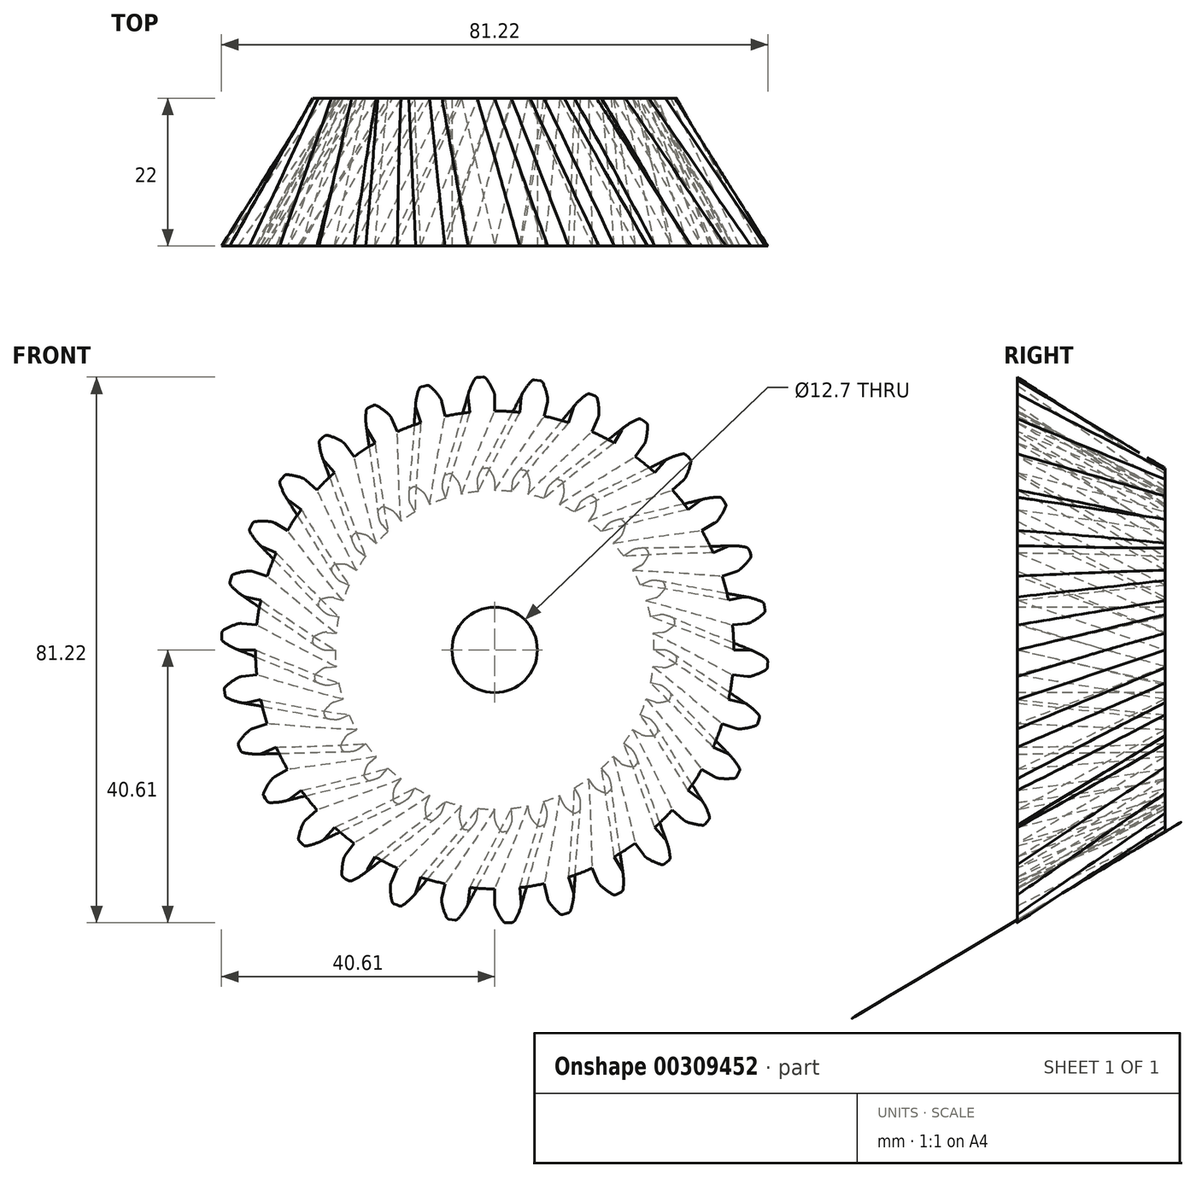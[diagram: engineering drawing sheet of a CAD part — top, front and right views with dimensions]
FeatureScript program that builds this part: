
annotation { "Feature Type Name" : "Feature", "Feature Type Description" : "" }
export const myFeature = defineFeature(function(context is Context, id is Id, definition is map)
    precondition{}
    {
        {
            var Q0;
            Q0=qCreatedBy(makeId("Front.planeOp"),FACE);
            var sketch = newSketch(context, id + "F0", { "sketchPlane" : qUnion([Q0])});
            skCircle(sketch, "E0", {"center": v(0, 0) * mm, "radius": 23.71 * mm});
            skArc(sketch, "E1.trimOffspring", {"start": v(-0.14, 25.74) * mm, "mid": v(-0.44, 26.31) * mm, "end": v(-0.8, 26.85) * mm});
            skLineSegment(sketch, "E2", {"start": v(0, 25.08) * mm, "end": v(0, 23.71) * mm});
            skLineSegment(sketch, "E3", {"start": v(-1.22, 27.06) * mm, "end": v(-1.42, 27.06) * mm});
            skLineSegment(sketch, "E4.MirrorCS", {"start": v(-1.62, 27.04) * mm, "end": v(-1.42, 27.06) * mm});
            skArc(sketch, "E5.MirrorCS", {"start": v(-2.55, 25.61) * mm, "mid": v(-2.31, 26.22) * mm, "end": v(-2.02, 26.79) * mm});
            skLineSegment(sketch, "E6.MirrorCS", {"start": v(-2.62, 24.94) * mm, "end": v(-2.48, 23.58) * mm});
            skPoint(sketch, "E7.visualSharp", {"position": v(-2.66, 25.26) * mm});
            skArc(sketch, "E7.filletArc", {"start": v(-2.55, 25.61) * mm, "mid": v(-2.62, 25.28) * mm, "end": v(-2.62, 24.94) * mm});
            skPoint(sketch, "E8.visualSharp", {"position": v(0, 25.4) * mm});
            skArc(sketch, "E8.filletArc", {"start": v(0, 25.08) * mm, "mid": v(-0.04, 25.42) * mm, "end": v(-0.14, 25.74) * mm});
            skPoint(sketch, "E9.visualSharp", {"position": v(-1.88, 27.02) * mm});
            skArc(sketch, "E9.filletArc", {"start": v(-1.62, 27.04) * mm, "mid": v(-1.85, 26.97) * mm, "end": v(-2.02, 26.79) * mm});
            skPoint(sketch, "E10.visualSharp", {"position": v(-0.96, 27.07) * mm});
            skArc(sketch, "E10.filletArc", {"start": v(-0.8, 26.85) * mm, "mid": v(-0.98, 27.01) * mm, "end": v(-1.22, 27.06) * mm});
            skSolve(sketch);
        }
        {
            var Q0;
            Q0=qCreatedBy(makeId("Front.planeOp"),FACE);
            cPlane(context, id + "F1", {"entities" : qUnion([Q0]), "cplaneType" : CPlaneType.OFFSET, "offset" : 22 * mm, "width" : 152.4 * mm, "height" : 152.4 * mm});
        }
        {
            var Q0;
            Q0=qCreatedBy(id+"F1.planeOp",FACE);
            var sketch = newSketch(context, id + "F2", { "sketchPlane" : qUnion([Q0])});
            skCircle(sketch, "E11", {"center": v(0, 0) * mm, "radius": 35.56 * mm});
            skArc(sketch, "E12.trimOffspring", {"start": v(-0.13, 38.42) * mm, "mid": v(-0.64, 39.44) * mm, "end": v(-1.28, 40.4) * mm});
            skLineSegment(sketch, "E13", {"start": v(0, 37.79) * mm, "end": v(0, 35.56) * mm});
            skLineSegment(sketch, "E14", {"start": v(-1.7, 40.6) * mm, "end": v(-2.13, 40.6) * mm});
            skLineSegment(sketch, "E15.MirrorCS", {"start": v(-2.55, 40.56) * mm, "end": v(-2.13, 40.6) * mm});
            skArc(sketch, "E16.MirrorCS", {"start": v(-3.89, 38.22) * mm, "mid": v(-3.48, 39.3) * mm, "end": v(-2.95, 40.31) * mm});
            skLineSegment(sketch, "E17.MirrorCS", {"start": v(-3.95, 37.58) * mm, "end": v(-3.72, 35.37) * mm});
            skPoint(sketch, "E18.visualSharp", {"position": v(-3.98, 37.9) * mm});
            skArc(sketch, "E18.filletArc", {"start": v(-3.89, 38.22) * mm, "mid": v(-3.95, 37.9) * mm, "end": v(-3.95, 37.58) * mm});
            skPoint(sketch, "E19.visualSharp", {"position": v(0, 38.1) * mm});
            skArc(sketch, "E19.filletArc", {"start": v(0, 37.79) * mm, "mid": v(-0.03, 38.1) * mm, "end": v(-0.13, 38.42) * mm});
            skPoint(sketch, "E20.visualSharp", {"position": v(-2.81, 40.54) * mm});
            skArc(sketch, "E20.filletArc", {"start": v(-2.55, 40.56) * mm, "mid": v(-2.78, 40.49) * mm, "end": v(-2.95, 40.31) * mm});
            skPoint(sketch, "E21.visualSharp", {"position": v(-1.44, 40.61) * mm});
            skArc(sketch, "E21.filletArc", {"start": v(-1.28, 40.4) * mm, "mid": v(-1.46, 40.56) * mm, "end": v(-1.7, 40.6) * mm});
            skLineSegment(sketch, "E22.1.0", {"start": v(-10.93, 39.14) * mm, "end": v(-10.52, 39.26) * mm});
            skLineSegment(sketch, "E22.1.1", {"start": v(-10.1, 39.36) * mm, "end": v(-10.52, 39.26) * mm});
            skArc(sketch, "E22.1.2", {"start": v(-9.65, 39.25) * mm, "mid": v(-9.86, 39.37) * mm, "end": v(-10.1, 39.36) * mm});
            skArc(sketch, "E22.1.3", {"start": v(-10.93, 39.14) * mm, "mid": v(-11.14, 39.02) * mm, "end": v(-11.27, 38.82) * mm});
            skArc(sketch, "E22.1.4", {"start": v(-11.75, 36.58) * mm, "mid": v(-11.58, 37.71) * mm, "end": v(-11.27, 38.82) * mm});
            skArc(sketch, "E22.1.5", {"start": v(-8.11, 37.55) * mm, "mid": v(-8.83, 38.45) * mm, "end": v(-9.65, 39.25) * mm});
            skArc(sketch, "E22.1.6", {"start": v(-7.86, 36.96) * mm, "mid": v(-7.95, 37.27) * mm, "end": v(-8.11, 37.55) * mm});
            skArc(sketch, "E22.1.7", {"start": v(-11.75, 36.58) * mm, "mid": v(-11.75, 36.25) * mm, "end": v(-11.68, 35.94) * mm});
            skLineSegment(sketch, "E22.1.8", {"start": v(-11.68, 35.94) * mm, "end": v(-10.99, 33.82) * mm});
            skLineSegment(sketch, "E22.1.9", {"start": v(-7.86, 36.96) * mm, "end": v(-7.4, 34.78) * mm});
            skLineSegment(sketch, "E22.2.0", {"start": v(-18.83, 36.01) * mm, "end": v(-18.45, 36.22) * mm});
            skLineSegment(sketch, "E22.2.1", {"start": v(-18.07, 36.4) * mm, "end": v(-18.45, 36.22) * mm});
            skArc(sketch, "E22.2.2", {"start": v(-17.6, 36.4) * mm, "mid": v(-17.83, 36.45) * mm, "end": v(-18.07, 36.4) * mm});
            skArc(sketch, "E22.2.3", {"start": v(-18.83, 36.01) * mm, "mid": v(-19.01, 35.85) * mm, "end": v(-19.1, 35.63) * mm});
            skArc(sketch, "E22.2.4", {"start": v(-19.1, 33.33) * mm, "mid": v(-19.17, 34.48) * mm, "end": v(-19.1, 35.63) * mm});
            skArc(sketch, "E22.2.5", {"start": v(-15.74, 35.04) * mm, "mid": v(-16.63, 35.77) * mm, "end": v(-17.6, 36.4) * mm});
            skArc(sketch, "E22.2.6", {"start": v(-15.37, 34.52) * mm, "mid": v(-15.53, 34.8) * mm, "end": v(-15.74, 35.04) * mm});
            skArc(sketch, "E22.2.7", {"start": v(-19.1, 33.33) * mm, "mid": v(-19.03, 33.02) * mm, "end": v(-18.9, 32.73) * mm});
            skLineSegment(sketch, "E22.2.8", {"start": v(-18.9, 32.73) * mm, "end": v(-17.78, 30.8) * mm});
            skLineSegment(sketch, "E22.2.9", {"start": v(-15.37, 34.52) * mm, "end": v(-14.46, 32.49) * mm});
            skLineSegment(sketch, "E22.3.0", {"start": v(-25.9, 31.31) * mm, "end": v(-25.58, 31.59) * mm});
            skLineSegment(sketch, "E22.3.1", {"start": v(-25.24, 31.85) * mm, "end": v(-25.58, 31.59) * mm});
            skArc(sketch, "E22.3.2", {"start": v(-24.78, 31.94) * mm, "mid": v(-25.02, 31.95) * mm, "end": v(-25.24, 31.85) * mm});
            skArc(sketch, "E22.3.3", {"start": v(-25.9, 31.31) * mm, "mid": v(-26.05, 31.12) * mm, "end": v(-26.09, 30.88) * mm});
            skArc(sketch, "E22.3.4", {"start": v(-25.61, 28.63) * mm, "mid": v(-25.92, 29.74) * mm, "end": v(-26.09, 30.88) * mm});
            skArc(sketch, "E22.3.5", {"start": v(-22.68, 31) * mm, "mid": v(-23.7, 31.53) * mm, "end": v(-24.78, 31.94) * mm});
            skArc(sketch, "E22.3.6", {"start": v(-22.21, 30.57) * mm, "mid": v(-22.43, 30.81) * mm, "end": v(-22.68, 31) * mm});
            skArc(sketch, "E22.3.7", {"start": v(-25.61, 28.63) * mm, "mid": v(-25.48, 28.34) * mm, "end": v(-25.29, 28.08) * mm});
            skLineSegment(sketch, "E22.3.8", {"start": v(-25.29, 28.08) * mm, "end": v(-23.8, 26.43) * mm});
            skLineSegment(sketch, "E22.3.9", {"start": v(-22.21, 30.57) * mm, "end": v(-20.9, 28.77) * mm});
            skLineSegment(sketch, "E22.4.0", {"start": v(-31.85, 25.24) * mm, "end": v(-31.59, 25.58) * mm});
            skLineSegment(sketch, "E22.4.1", {"start": v(-31.31, 25.9) * mm, "end": v(-31.59, 25.58) * mm});
            skArc(sketch, "E22.4.2", {"start": v(-30.88, 26.09) * mm, "mid": v(-31.12, 26.05) * mm, "end": v(-31.31, 25.9) * mm});
            skArc(sketch, "E22.4.3", {"start": v(-31.85, 25.24) * mm, "mid": v(-31.95, 25.02) * mm, "end": v(-31.94, 24.78) * mm});
            skArc(sketch, "E22.4.4", {"start": v(-31, 22.68) * mm, "mid": v(-31.53, 23.7) * mm, "end": v(-31.94, 24.78) * mm});
            skArc(sketch, "E22.4.5", {"start": v(-28.63, 25.61) * mm, "mid": v(-29.74, 25.92) * mm, "end": v(-30.88, 26.09) * mm});
            skArc(sketch, "E22.4.6", {"start": v(-28.08, 25.29) * mm, "mid": v(-28.34, 25.48) * mm, "end": v(-28.63, 25.61) * mm});
            skArc(sketch, "E22.4.7", {"start": v(-31, 22.68) * mm, "mid": v(-30.81, 22.43) * mm, "end": v(-30.57, 22.21) * mm});
            skLineSegment(sketch, "E22.4.8", {"start": v(-30.57, 22.21) * mm, "end": v(-28.77, 20.9) * mm});
            skLineSegment(sketch, "E22.4.9", {"start": v(-28.08, 25.29) * mm, "end": v(-26.43, 23.8) * mm});
            skLineSegment(sketch, "E22.5.0", {"start": v(-36.4, 18.07) * mm, "end": v(-36.22, 18.45) * mm});
            skLineSegment(sketch, "E22.5.1", {"start": v(-36.01, 18.83) * mm, "end": v(-36.22, 18.45) * mm});
            skArc(sketch, "E22.5.2", {"start": v(-35.63, 19.1) * mm, "mid": v(-35.85, 19.01) * mm, "end": v(-36.01, 18.83) * mm});
            skArc(sketch, "E22.5.3", {"start": v(-36.4, 18.07) * mm, "mid": v(-36.45, 17.83) * mm, "end": v(-36.4, 17.6) * mm});
            skArc(sketch, "E22.5.4", {"start": v(-35.04, 15.74) * mm, "mid": v(-35.77, 16.63) * mm, "end": v(-36.4, 17.6) * mm});
            skArc(sketch, "E22.5.5", {"start": v(-33.33, 19.1) * mm, "mid": v(-34.48, 19.17) * mm, "end": v(-35.63, 19.1) * mm});
            skArc(sketch, "E22.5.6", {"start": v(-32.73, 18.9) * mm, "mid": v(-33.02, 19.03) * mm, "end": v(-33.33, 19.1) * mm});
            skArc(sketch, "E22.5.7", {"start": v(-35.04, 15.74) * mm, "mid": v(-34.8, 15.53) * mm, "end": v(-34.52, 15.37) * mm});
            skLineSegment(sketch, "E22.5.8", {"start": v(-34.52, 15.37) * mm, "end": v(-32.49, 14.46) * mm});
            skLineSegment(sketch, "E22.5.9", {"start": v(-32.73, 18.9) * mm, "end": v(-30.8, 17.78) * mm});
            skLineSegment(sketch, "E22.6.0", {"start": v(-39.36, 10.1) * mm, "end": v(-39.26, 10.52) * mm});
            skLineSegment(sketch, "E22.6.1", {"start": v(-39.14, 10.93) * mm, "end": v(-39.26, 10.52) * mm});
            skArc(sketch, "E22.6.2", {"start": v(-38.82, 11.27) * mm, "mid": v(-39.02, 11.14) * mm, "end": v(-39.14, 10.93) * mm});
            skArc(sketch, "E22.6.3", {"start": v(-39.36, 10.1) * mm, "mid": v(-39.37, 9.86) * mm, "end": v(-39.25, 9.65) * mm});
            skArc(sketch, "E22.6.4", {"start": v(-37.55, 8.11) * mm, "mid": v(-38.45, 8.83) * mm, "end": v(-39.25, 9.65) * mm});
            skArc(sketch, "E22.6.5", {"start": v(-36.58, 11.75) * mm, "mid": v(-37.71, 11.58) * mm, "end": v(-38.82, 11.27) * mm});
            skArc(sketch, "E22.6.6", {"start": v(-35.94, 11.68) * mm, "mid": v(-36.25, 11.75) * mm, "end": v(-36.58, 11.75) * mm});
            skArc(sketch, "E22.6.7", {"start": v(-37.55, 8.11) * mm, "mid": v(-37.27, 7.95) * mm, "end": v(-36.96, 7.86) * mm});
            skLineSegment(sketch, "E22.6.8", {"start": v(-36.96, 7.86) * mm, "end": v(-34.78, 7.4) * mm});
            skLineSegment(sketch, "E22.6.9", {"start": v(-35.94, 11.68) * mm, "end": v(-33.82, 10.99) * mm});
            skLineSegment(sketch, "E22.7.0", {"start": v(-40.6, 1.7) * mm, "end": v(-40.6, 2.13) * mm});
            skLineSegment(sketch, "E22.7.1", {"start": v(-40.56, 2.55) * mm, "end": v(-40.6, 2.13) * mm});
            skArc(sketch, "E22.7.2", {"start": v(-40.31, 2.95) * mm, "mid": v(-40.49, 2.78) * mm, "end": v(-40.56, 2.55) * mm});
            skArc(sketch, "E22.7.3", {"start": v(-40.6, 1.7) * mm, "mid": v(-40.56, 1.46) * mm, "end": v(-40.4, 1.28) * mm});
            skArc(sketch, "E22.7.4", {"start": v(-38.42, 0.13) * mm, "mid": v(-39.44, 0.64) * mm, "end": v(-40.4, 1.28) * mm});
            skArc(sketch, "E22.7.5", {"start": v(-38.22, 3.89) * mm, "mid": v(-39.3, 3.48) * mm, "end": v(-40.31, 2.95) * mm});
            skArc(sketch, "E22.7.6", {"start": v(-37.58, 3.95) * mm, "mid": v(-37.9, 3.95) * mm, "end": v(-38.22, 3.89) * mm});
            skArc(sketch, "E22.7.7", {"start": v(-38.42, 0.13) * mm, "mid": v(-38.1, 0.03) * mm, "end": v(-37.79, 0) * mm});
            skLineSegment(sketch, "E22.7.8", {"start": v(-37.79, 0) * mm, "end": v(-35.56, 0) * mm});
            skLineSegment(sketch, "E22.7.9", {"start": v(-37.58, 3.95) * mm, "end": v(-35.37, 3.72) * mm});
            skLineSegment(sketch, "E22.8.0", {"start": v(-40.07, -6.78) * mm, "end": v(-40.15, -6.36) * mm});
            skLineSegment(sketch, "E22.8.1", {"start": v(-40.2, -5.93) * mm, "end": v(-40.15, -6.36) * mm});
            skArc(sketch, "E22.8.2", {"start": v(-40.05, -5.5) * mm, "mid": v(-40.18, -5.7) * mm, "end": v(-40.2, -5.93) * mm});
            skArc(sketch, "E22.8.3", {"start": v(-40.07, -6.78) * mm, "mid": v(-39.97, -7) * mm, "end": v(-39.79, -7.15) * mm});
            skArc(sketch, "E22.8.4", {"start": v(-37.6, -7.86) * mm, "mid": v(-38.72, -7.57) * mm, "end": v(-39.79, -7.15) * mm});
            skArc(sketch, "E22.8.5", {"start": v(-38.2, -4.14) * mm, "mid": v(-39.16, -4.76) * mm, "end": v(-40.05, -5.5) * mm});
            skArc(sketch, "E22.8.6", {"start": v(-37.58, -3.95) * mm, "mid": v(-37.9, -4.02) * mm, "end": v(-38.2, -4.14) * mm});
            skArc(sketch, "E22.8.7", {"start": v(-37.6, -7.86) * mm, "mid": v(-37.28, -7.9) * mm, "end": v(-36.96, -7.86) * mm});
            skLineSegment(sketch, "E22.8.8", {"start": v(-36.96, -7.86) * mm, "end": v(-34.78, -7.4) * mm});
            skLineSegment(sketch, "E22.8.9", {"start": v(-37.58, -3.95) * mm, "end": v(-35.37, -3.72) * mm});
            skLineSegment(sketch, "E22.9.0", {"start": v(-37.79, -14.96) * mm, "end": v(-37.95, -14.57) * mm});
            skLineSegment(sketch, "E22.9.1", {"start": v(-38.1, -14.16) * mm, "end": v(-37.95, -14.57) * mm});
            skArc(sketch, "E22.9.2", {"start": v(-38.03, -13.7) * mm, "mid": v(-38.12, -13.92) * mm, "end": v(-38.1, -14.16) * mm});
            skArc(sketch, "E22.9.3", {"start": v(-37.79, -14.96) * mm, "mid": v(-37.64, -15.16) * mm, "end": v(-37.43, -15.27) * mm});
            skArc(sketch, "E22.9.4", {"start": v(-35.15, -15.5) * mm, "mid": v(-36.3, -15.46) * mm, "end": v(-37.43, -15.27) * mm});
            skArc(sketch, "E22.9.5", {"start": v(-36.5, -12) * mm, "mid": v(-37.32, -12.8) * mm, "end": v(-38.03, -13.7) * mm});
            skArc(sketch, "E22.9.6", {"start": v(-35.94, -11.68) * mm, "mid": v(-36.23, -11.8) * mm, "end": v(-36.5, -12) * mm});
            skArc(sketch, "E22.9.7", {"start": v(-35.15, -15.5) * mm, "mid": v(-34.83, -15.47) * mm, "end": v(-34.52, -15.37) * mm});
            skLineSegment(sketch, "E22.9.8", {"start": v(-34.52, -15.37) * mm, "end": v(-32.49, -14.46) * mm});
            skLineSegment(sketch, "E22.9.9", {"start": v(-35.94, -11.68) * mm, "end": v(-33.82, -10.99) * mm});
            skLineSegment(sketch, "E22.10.0", {"start": v(-33.85, -22.5) * mm, "end": v(-34.09, -22.14) * mm});
            skLineSegment(sketch, "E22.10.1", {"start": v(-34.32, -21.77) * mm, "end": v(-34.09, -22.14) * mm});
            skArc(sketch, "E22.10.2", {"start": v(-34.35, -21.3) * mm, "mid": v(-34.4, -21.54) * mm, "end": v(-34.32, -21.77) * mm});
            skArc(sketch, "E22.10.3", {"start": v(-33.85, -22.5) * mm, "mid": v(-33.67, -22.66) * mm, "end": v(-33.44, -22.72) * mm});
            skArc(sketch, "E22.10.4", {"start": v(-31.15, -22.48) * mm, "mid": v(-32.29, -22.67) * mm, "end": v(-33.44, -22.72) * mm});
            skArc(sketch, "E22.10.5", {"start": v(-33.2, -19.32) * mm, "mid": v(-33.84, -20.28) * mm, "end": v(-34.35, -21.3) * mm});
            skArc(sketch, "E22.10.6", {"start": v(-32.73, -18.9) * mm, "mid": v(-32.99, -19.08) * mm, "end": v(-33.2, -19.32) * mm});
            skArc(sketch, "E22.10.7", {"start": v(-31.15, -22.48) * mm, "mid": v(-30.85, -22.37) * mm, "end": v(-30.57, -22.21) * mm});
            skLineSegment(sketch, "E22.10.8", {"start": v(-30.57, -22.21) * mm, "end": v(-28.77, -20.9) * mm});
            skLineSegment(sketch, "E22.10.9", {"start": v(-32.73, -18.9) * mm, "end": v(-30.8, -17.78) * mm});
            skLineSegment(sketch, "E22.11.0", {"start": v(-28.43, -29.04) * mm, "end": v(-28.74, -28.74) * mm});
            skLineSegment(sketch, "E22.11.1", {"start": v(-29.04, -28.43) * mm, "end": v(-28.74, -28.74) * mm});
            skArc(sketch, "E22.11.2", {"start": v(-29.17, -27.98) * mm, "mid": v(-29.16, -28.22) * mm, "end": v(-29.04, -28.43) * mm});
            skArc(sketch, "E22.11.3", {"start": v(-28.43, -29.04) * mm, "mid": v(-28.22, -29.16) * mm, "end": v(-27.98, -29.17) * mm});
            skArc(sketch, "E22.11.4", {"start": v(-25.8, -28.46) * mm, "mid": v(-26.87, -28.88) * mm, "end": v(-27.98, -29.17) * mm});
            skArc(sketch, "E22.11.5", {"start": v(-28.46, -25.8) * mm, "mid": v(-28.88, -26.87) * mm, "end": v(-29.17, -27.98) * mm});
            skArc(sketch, "E22.11.6", {"start": v(-28.08, -25.29) * mm, "mid": v(-28.3, -25.52) * mm, "end": v(-28.46, -25.8) * mm});
            skArc(sketch, "E22.11.7", {"start": v(-25.8, -28.46) * mm, "mid": v(-25.52, -28.3) * mm, "end": v(-25.29, -28.08) * mm});
            skLineSegment(sketch, "E22.11.8", {"start": v(-25.29, -28.08) * mm, "end": v(-23.8, -26.43) * mm});
            skLineSegment(sketch, "E22.11.9", {"start": v(-28.08, -25.29) * mm, "end": v(-26.43, -23.8) * mm});
            skLineSegment(sketch, "E22.12.0", {"start": v(-21.77, -34.32) * mm, "end": v(-22.14, -34.09) * mm});
            skLineSegment(sketch, "E22.12.1", {"start": v(-22.5, -33.85) * mm, "end": v(-22.14, -34.09) * mm});
            skArc(sketch, "E22.12.2", {"start": v(-22.72, -33.44) * mm, "mid": v(-22.66, -33.67) * mm, "end": v(-22.5, -33.85) * mm});
            skArc(sketch, "E22.12.3", {"start": v(-21.77, -34.32) * mm, "mid": v(-21.54, -34.4) * mm, "end": v(-21.3, -34.35) * mm});
            skArc(sketch, "E22.12.4", {"start": v(-19.32, -33.2) * mm, "mid": v(-20.28, -33.84) * mm, "end": v(-21.3, -34.35) * mm});
            skArc(sketch, "E22.12.5", {"start": v(-22.48, -31.15) * mm, "mid": v(-22.67, -32.29) * mm, "end": v(-22.72, -33.44) * mm});
            skArc(sketch, "E22.12.6", {"start": v(-22.21, -30.57) * mm, "mid": v(-22.37, -30.85) * mm, "end": v(-22.48, -31.15) * mm});
            skArc(sketch, "E22.12.7", {"start": v(-19.32, -33.2) * mm, "mid": v(-19.08, -32.99) * mm, "end": v(-18.9, -32.73) * mm});
            skLineSegment(sketch, "E22.12.8", {"start": v(-18.9, -32.73) * mm, "end": v(-17.78, -30.8) * mm});
            skLineSegment(sketch, "E22.12.9", {"start": v(-22.21, -30.57) * mm, "end": v(-20.9, -28.77) * mm});
            skLineSegment(sketch, "E22.13.0", {"start": v(-14.16, -38.1) * mm, "end": v(-14.57, -37.95) * mm});
            skLineSegment(sketch, "E22.13.1", {"start": v(-14.96, -37.79) * mm, "end": v(-14.57, -37.95) * mm});
            skArc(sketch, "E22.13.2", {"start": v(-15.27, -37.43) * mm, "mid": v(-15.16, -37.64) * mm, "end": v(-14.96, -37.79) * mm});
            skArc(sketch, "E22.13.3", {"start": v(-14.16, -38.1) * mm, "mid": v(-13.92, -38.12) * mm, "end": v(-13.7, -38.03) * mm});
            skArc(sketch, "E22.13.4", {"start": v(-12, -36.5) * mm, "mid": v(-12.8, -37.32) * mm, "end": v(-13.7, -38.03) * mm});
            skArc(sketch, "E22.13.5", {"start": v(-15.5, -35.15) * mm, "mid": v(-15.46, -36.3) * mm, "end": v(-15.27, -37.43) * mm});
            skArc(sketch, "E22.13.6", {"start": v(-15.37, -34.52) * mm, "mid": v(-15.47, -34.83) * mm, "end": v(-15.5, -35.15) * mm});
            skArc(sketch, "E22.13.7", {"start": v(-12, -36.5) * mm, "mid": v(-11.8, -36.23) * mm, "end": v(-11.68, -35.94) * mm});
            skLineSegment(sketch, "E22.13.8", {"start": v(-11.68, -35.94) * mm, "end": v(-10.99, -33.82) * mm});
            skLineSegment(sketch, "E22.13.9", {"start": v(-15.37, -34.52) * mm, "end": v(-14.46, -32.49) * mm});
            skLineSegment(sketch, "E22.14.0", {"start": v(-5.93, -40.2) * mm, "end": v(-6.36, -40.15) * mm});
            skLineSegment(sketch, "E22.14.1", {"start": v(-6.78, -40.07) * mm, "end": v(-6.36, -40.15) * mm});
            skArc(sketch, "E22.14.2", {"start": v(-7.15, -39.79) * mm, "mid": v(-7, -39.97) * mm, "end": v(-6.78, -40.07) * mm});
            skArc(sketch, "E22.14.3", {"start": v(-5.93, -40.2) * mm, "mid": v(-5.7, -40.18) * mm, "end": v(-5.5, -40.05) * mm});
            skArc(sketch, "E22.14.4", {"start": v(-4.14, -38.2) * mm, "mid": v(-4.76, -39.16) * mm, "end": v(-5.5, -40.05) * mm});
            skArc(sketch, "E22.14.5", {"start": v(-7.86, -37.6) * mm, "mid": v(-7.57, -38.72) * mm, "end": v(-7.15, -39.79) * mm});
            skArc(sketch, "E22.14.6", {"start": v(-7.86, -36.96) * mm, "mid": v(-7.9, -37.28) * mm, "end": v(-7.86, -37.6) * mm});
            skArc(sketch, "E22.14.7", {"start": v(-4.14, -38.2) * mm, "mid": v(-4.02, -37.9) * mm, "end": v(-3.95, -37.58) * mm});
            skLineSegment(sketch, "E22.14.8", {"start": v(-3.95, -37.58) * mm, "end": v(-3.72, -35.37) * mm});
            skLineSegment(sketch, "E22.14.9", {"start": v(-7.86, -36.96) * mm, "end": v(-7.4, -34.78) * mm});
            skLineSegment(sketch, "E22.15.0", {"start": v(2.55, -40.56) * mm, "end": v(2.13, -40.6) * mm});
            skLineSegment(sketch, "E22.15.1", {"start": v(1.7, -40.6) * mm, "end": v(2.13, -40.6) * mm});
            skArc(sketch, "E22.15.2", {"start": v(1.28, -40.4) * mm, "mid": v(1.46, -40.56) * mm, "end": v(1.7, -40.6) * mm});
            skArc(sketch, "E22.15.3", {"start": v(2.55, -40.56) * mm, "mid": v(2.78, -40.49) * mm, "end": v(2.95, -40.31) * mm});
            skArc(sketch, "E22.15.4", {"start": v(3.89, -38.22) * mm, "mid": v(3.48, -39.3) * mm, "end": v(2.95, -40.31) * mm});
            skArc(sketch, "E22.15.5", {"start": v(0.13, -38.42) * mm, "mid": v(0.64, -39.44) * mm, "end": v(1.28, -40.4) * mm});
            skArc(sketch, "E22.15.6", {"start": v(0, -37.79) * mm, "mid": v(0.03, -38.1) * mm, "end": v(0.13, -38.42) * mm});
            skArc(sketch, "E22.15.7", {"start": v(3.89, -38.22) * mm, "mid": v(3.95, -37.9) * mm, "end": v(3.95, -37.58) * mm});
            skLineSegment(sketch, "E22.15.8", {"start": v(3.95, -37.58) * mm, "end": v(3.72, -35.37) * mm});
            skLineSegment(sketch, "E22.15.9", {"start": v(0, -37.79) * mm, "end": v(0, -35.56) * mm});
            skLineSegment(sketch, "E22.16.0", {"start": v(10.93, -39.14) * mm, "end": v(10.52, -39.26) * mm});
            skLineSegment(sketch, "E22.16.1", {"start": v(10.1, -39.36) * mm, "end": v(10.52, -39.26) * mm});
            skArc(sketch, "E22.16.2", {"start": v(9.65, -39.25) * mm, "mid": v(9.86, -39.37) * mm, "end": v(10.1, -39.36) * mm});
            skArc(sketch, "E22.16.3", {"start": v(10.93, -39.14) * mm, "mid": v(11.14, -39.02) * mm, "end": v(11.27, -38.82) * mm});
            skArc(sketch, "E22.16.4", {"start": v(11.75, -36.58) * mm, "mid": v(11.58, -37.71) * mm, "end": v(11.27, -38.82) * mm});
            skArc(sketch, "E22.16.5", {"start": v(8.11, -37.55) * mm, "mid": v(8.83, -38.45) * mm, "end": v(9.65, -39.25) * mm});
            skArc(sketch, "E22.16.6", {"start": v(7.86, -36.96) * mm, "mid": v(7.95, -37.27) * mm, "end": v(8.11, -37.55) * mm});
            skArc(sketch, "E22.16.7", {"start": v(11.75, -36.58) * mm, "mid": v(11.75, -36.25) * mm, "end": v(11.68, -35.94) * mm});
            skLineSegment(sketch, "E22.16.8", {"start": v(11.68, -35.94) * mm, "end": v(10.99, -33.82) * mm});
            skLineSegment(sketch, "E22.16.9", {"start": v(7.86, -36.96) * mm, "end": v(7.4, -34.78) * mm});
            skLineSegment(sketch, "E22.17.0", {"start": v(18.83, -36.01) * mm, "end": v(18.45, -36.22) * mm});
            skLineSegment(sketch, "E22.17.1", {"start": v(18.07, -36.4) * mm, "end": v(18.45, -36.22) * mm});
            skArc(sketch, "E22.17.2", {"start": v(17.6, -36.4) * mm, "mid": v(17.83, -36.45) * mm, "end": v(18.07, -36.4) * mm});
            skArc(sketch, "E22.17.3", {"start": v(18.83, -36.01) * mm, "mid": v(19.01, -35.85) * mm, "end": v(19.1, -35.63) * mm});
            skArc(sketch, "E22.17.4", {"start": v(19.1, -33.33) * mm, "mid": v(19.17, -34.48) * mm, "end": v(19.1, -35.63) * mm});
            skArc(sketch, "E22.17.5", {"start": v(15.74, -35.04) * mm, "mid": v(16.63, -35.77) * mm, "end": v(17.6, -36.4) * mm});
            skArc(sketch, "E22.17.6", {"start": v(15.37, -34.52) * mm, "mid": v(15.53, -34.8) * mm, "end": v(15.74, -35.04) * mm});
            skArc(sketch, "E22.17.7", {"start": v(19.1, -33.33) * mm, "mid": v(19.03, -33.02) * mm, "end": v(18.9, -32.73) * mm});
            skLineSegment(sketch, "E22.17.8", {"start": v(18.9, -32.73) * mm, "end": v(17.78, -30.8) * mm});
            skLineSegment(sketch, "E22.17.9", {"start": v(15.37, -34.52) * mm, "end": v(14.46, -32.49) * mm});
            skLineSegment(sketch, "E22.18.0", {"start": v(25.9, -31.31) * mm, "end": v(25.58, -31.59) * mm});
            skLineSegment(sketch, "E22.18.1", {"start": v(25.24, -31.85) * mm, "end": v(25.58, -31.59) * mm});
            skArc(sketch, "E22.18.2", {"start": v(24.78, -31.94) * mm, "mid": v(25.02, -31.95) * mm, "end": v(25.24, -31.85) * mm});
            skArc(sketch, "E22.18.3", {"start": v(25.9, -31.31) * mm, "mid": v(26.05, -31.12) * mm, "end": v(26.09, -30.88) * mm});
            skArc(sketch, "E22.18.4", {"start": v(25.61, -28.63) * mm, "mid": v(25.92, -29.74) * mm, "end": v(26.09, -30.88) * mm});
            skArc(sketch, "E22.18.5", {"start": v(22.68, -31) * mm, "mid": v(23.7, -31.53) * mm, "end": v(24.78, -31.94) * mm});
            skArc(sketch, "E22.18.6", {"start": v(22.21, -30.57) * mm, "mid": v(22.43, -30.81) * mm, "end": v(22.68, -31) * mm});
            skArc(sketch, "E22.18.7", {"start": v(25.61, -28.63) * mm, "mid": v(25.48, -28.34) * mm, "end": v(25.29, -28.08) * mm});
            skLineSegment(sketch, "E22.18.8", {"start": v(25.29, -28.08) * mm, "end": v(23.8, -26.43) * mm});
            skLineSegment(sketch, "E22.18.9", {"start": v(22.21, -30.57) * mm, "end": v(20.9, -28.77) * mm});
            skLineSegment(sketch, "E22.19.0", {"start": v(31.85, -25.24) * mm, "end": v(31.59, -25.58) * mm});
            skLineSegment(sketch, "E22.19.1", {"start": v(31.31, -25.9) * mm, "end": v(31.59, -25.58) * mm});
            skArc(sketch, "E22.19.2", {"start": v(30.88, -26.09) * mm, "mid": v(31.12, -26.05) * mm, "end": v(31.31, -25.9) * mm});
            skArc(sketch, "E22.19.3", {"start": v(31.85, -25.24) * mm, "mid": v(31.95, -25.02) * mm, "end": v(31.94, -24.78) * mm});
            skArc(sketch, "E22.19.4", {"start": v(31, -22.68) * mm, "mid": v(31.53, -23.7) * mm, "end": v(31.94, -24.78) * mm});
            skArc(sketch, "E22.19.5", {"start": v(28.63, -25.61) * mm, "mid": v(29.74, -25.92) * mm, "end": v(30.88, -26.09) * mm});
            skArc(sketch, "E22.19.6", {"start": v(28.08, -25.29) * mm, "mid": v(28.34, -25.48) * mm, "end": v(28.63, -25.61) * mm});
            skArc(sketch, "E22.19.7", {"start": v(31, -22.68) * mm, "mid": v(30.81, -22.43) * mm, "end": v(30.57, -22.21) * mm});
            skLineSegment(sketch, "E22.19.8", {"start": v(30.57, -22.21) * mm, "end": v(28.77, -20.9) * mm});
            skLineSegment(sketch, "E22.19.9", {"start": v(28.08, -25.29) * mm, "end": v(26.43, -23.8) * mm});
            skLineSegment(sketch, "E22.20.0", {"start": v(36.4, -18.07) * mm, "end": v(36.22, -18.45) * mm});
            skLineSegment(sketch, "E22.20.1", {"start": v(36.01, -18.83) * mm, "end": v(36.22, -18.45) * mm});
            skArc(sketch, "E22.20.2", {"start": v(35.63, -19.1) * mm, "mid": v(35.85, -19.01) * mm, "end": v(36.01, -18.83) * mm});
            skArc(sketch, "E22.20.3", {"start": v(36.4, -18.07) * mm, "mid": v(36.45, -17.83) * mm, "end": v(36.4, -17.6) * mm});
            skArc(sketch, "E22.20.4", {"start": v(35.04, -15.74) * mm, "mid": v(35.77, -16.63) * mm, "end": v(36.4, -17.6) * mm});
            skArc(sketch, "E22.20.5", {"start": v(33.33, -19.1) * mm, "mid": v(34.48, -19.17) * mm, "end": v(35.63, -19.1) * mm});
            skArc(sketch, "E22.20.6", {"start": v(32.73, -18.9) * mm, "mid": v(33.02, -19.03) * mm, "end": v(33.33, -19.1) * mm});
            skArc(sketch, "E22.20.7", {"start": v(35.04, -15.74) * mm, "mid": v(34.8, -15.53) * mm, "end": v(34.52, -15.37) * mm});
            skLineSegment(sketch, "E22.20.8", {"start": v(34.52, -15.37) * mm, "end": v(32.49, -14.46) * mm});
            skLineSegment(sketch, "E22.20.9", {"start": v(32.73, -18.9) * mm, "end": v(30.8, -17.78) * mm});
            skLineSegment(sketch, "E22.21.0", {"start": v(39.36, -10.1) * mm, "end": v(39.26, -10.52) * mm});
            skLineSegment(sketch, "E22.21.1", {"start": v(39.14, -10.93) * mm, "end": v(39.26, -10.52) * mm});
            skArc(sketch, "E22.21.2", {"start": v(38.82, -11.27) * mm, "mid": v(39.02, -11.14) * mm, "end": v(39.14, -10.93) * mm});
            skArc(sketch, "E22.21.3", {"start": v(39.36, -10.1) * mm, "mid": v(39.37, -9.86) * mm, "end": v(39.25, -9.65) * mm});
            skArc(sketch, "E22.21.4", {"start": v(37.55, -8.11) * mm, "mid": v(38.45, -8.83) * mm, "end": v(39.25, -9.65) * mm});
            skArc(sketch, "E22.21.5", {"start": v(36.58, -11.75) * mm, "mid": v(37.71, -11.58) * mm, "end": v(38.82, -11.27) * mm});
            skArc(sketch, "E22.21.6", {"start": v(35.94, -11.68) * mm, "mid": v(36.25, -11.75) * mm, "end": v(36.58, -11.75) * mm});
            skArc(sketch, "E22.21.7", {"start": v(37.55, -8.11) * mm, "mid": v(37.27, -7.95) * mm, "end": v(36.96, -7.86) * mm});
            skLineSegment(sketch, "E22.21.8", {"start": v(36.96, -7.86) * mm, "end": v(34.78, -7.4) * mm});
            skLineSegment(sketch, "E22.21.9", {"start": v(35.94, -11.68) * mm, "end": v(33.82, -10.99) * mm});
            skLineSegment(sketch, "E22.22.0", {"start": v(40.6, -1.7) * mm, "end": v(40.6, -2.13) * mm});
            skLineSegment(sketch, "E22.22.1", {"start": v(40.56, -2.55) * mm, "end": v(40.6, -2.13) * mm});
            skArc(sketch, "E22.22.2", {"start": v(40.31, -2.95) * mm, "mid": v(40.49, -2.78) * mm, "end": v(40.56, -2.55) * mm});
            skArc(sketch, "E22.22.3", {"start": v(40.6, -1.7) * mm, "mid": v(40.56, -1.46) * mm, "end": v(40.4, -1.28) * mm});
            skArc(sketch, "E22.22.4", {"start": v(38.42, -0.13) * mm, "mid": v(39.44, -0.64) * mm, "end": v(40.4, -1.28) * mm});
            skArc(sketch, "E22.22.5", {"start": v(38.22, -3.89) * mm, "mid": v(39.3, -3.48) * mm, "end": v(40.31, -2.95) * mm});
            skArc(sketch, "E22.22.6", {"start": v(37.58, -3.95) * mm, "mid": v(37.9, -3.95) * mm, "end": v(38.22, -3.89) * mm});
            skArc(sketch, "E22.22.7", {"start": v(38.42, -0.13) * mm, "mid": v(38.1, -0.03) * mm, "end": v(37.79, 0) * mm});
            skLineSegment(sketch, "E22.22.8", {"start": v(37.79, 0) * mm, "end": v(35.56, 0) * mm});
            skLineSegment(sketch, "E22.22.9", {"start": v(37.58, -3.95) * mm, "end": v(35.37, -3.72) * mm});
            skLineSegment(sketch, "E22.23.0", {"start": v(40.07, 6.78) * mm, "end": v(40.15, 6.36) * mm});
            skLineSegment(sketch, "E22.23.1", {"start": v(40.2, 5.93) * mm, "end": v(40.15, 6.36) * mm});
            skArc(sketch, "E22.23.2", {"start": v(40.05, 5.5) * mm, "mid": v(40.18, 5.7) * mm, "end": v(40.2, 5.93) * mm});
            skArc(sketch, "E22.23.3", {"start": v(40.07, 6.78) * mm, "mid": v(39.97, 7) * mm, "end": v(39.79, 7.15) * mm});
            skArc(sketch, "E22.23.4", {"start": v(37.6, 7.86) * mm, "mid": v(38.72, 7.57) * mm, "end": v(39.79, 7.15) * mm});
            skArc(sketch, "E22.23.5", {"start": v(38.2, 4.14) * mm, "mid": v(39.16, 4.76) * mm, "end": v(40.05, 5.5) * mm});
            skArc(sketch, "E22.23.6", {"start": v(37.58, 3.95) * mm, "mid": v(37.9, 4.02) * mm, "end": v(38.2, 4.14) * mm});
            skArc(sketch, "E22.23.7", {"start": v(37.6, 7.86) * mm, "mid": v(37.28, 7.9) * mm, "end": v(36.96, 7.86) * mm});
            skLineSegment(sketch, "E22.23.8", {"start": v(36.96, 7.86) * mm, "end": v(34.78, 7.4) * mm});
            skLineSegment(sketch, "E22.23.9", {"start": v(37.58, 3.95) * mm, "end": v(35.37, 3.72) * mm});
            skLineSegment(sketch, "E22.24.0", {"start": v(37.79, 14.96) * mm, "end": v(37.95, 14.57) * mm});
            skLineSegment(sketch, "E22.24.1", {"start": v(38.1, 14.16) * mm, "end": v(37.95, 14.57) * mm});
            skArc(sketch, "E22.24.2", {"start": v(38.03, 13.7) * mm, "mid": v(38.12, 13.92) * mm, "end": v(38.1, 14.16) * mm});
            skArc(sketch, "E22.24.3", {"start": v(37.79, 14.96) * mm, "mid": v(37.64, 15.16) * mm, "end": v(37.43, 15.27) * mm});
            skArc(sketch, "E22.24.4", {"start": v(35.15, 15.5) * mm, "mid": v(36.3, 15.46) * mm, "end": v(37.43, 15.27) * mm});
            skArc(sketch, "E22.24.5", {"start": v(36.5, 12) * mm, "mid": v(37.32, 12.8) * mm, "end": v(38.03, 13.7) * mm});
            skArc(sketch, "E22.24.6", {"start": v(35.94, 11.68) * mm, "mid": v(36.23, 11.8) * mm, "end": v(36.5, 12) * mm});
            skArc(sketch, "E22.24.7", {"start": v(35.15, 15.5) * mm, "mid": v(34.83, 15.47) * mm, "end": v(34.52, 15.37) * mm});
            skLineSegment(sketch, "E22.24.8", {"start": v(34.52, 15.37) * mm, "end": v(32.49, 14.46) * mm});
            skLineSegment(sketch, "E22.24.9", {"start": v(35.94, 11.68) * mm, "end": v(33.82, 10.99) * mm});
            skLineSegment(sketch, "E22.25.0", {"start": v(33.85, 22.5) * mm, "end": v(34.09, 22.14) * mm});
            skLineSegment(sketch, "E22.25.1", {"start": v(34.32, 21.77) * mm, "end": v(34.09, 22.14) * mm});
            skArc(sketch, "E22.25.2", {"start": v(34.35, 21.3) * mm, "mid": v(34.4, 21.54) * mm, "end": v(34.32, 21.77) * mm});
            skArc(sketch, "E22.25.3", {"start": v(33.85, 22.5) * mm, "mid": v(33.67, 22.66) * mm, "end": v(33.44, 22.72) * mm});
            skArc(sketch, "E22.25.4", {"start": v(31.15, 22.48) * mm, "mid": v(32.29, 22.67) * mm, "end": v(33.44, 22.72) * mm});
            skArc(sketch, "E22.25.5", {"start": v(33.2, 19.32) * mm, "mid": v(33.84, 20.28) * mm, "end": v(34.35, 21.3) * mm});
            skArc(sketch, "E22.25.6", {"start": v(32.73, 18.9) * mm, "mid": v(32.99, 19.08) * mm, "end": v(33.2, 19.32) * mm});
            skArc(sketch, "E22.25.7", {"start": v(31.15, 22.48) * mm, "mid": v(30.85, 22.37) * mm, "end": v(30.57, 22.21) * mm});
            skLineSegment(sketch, "E22.25.8", {"start": v(30.57, 22.21) * mm, "end": v(28.77, 20.9) * mm});
            skLineSegment(sketch, "E22.25.9", {"start": v(32.73, 18.9) * mm, "end": v(30.8, 17.78) * mm});
            skLineSegment(sketch, "E22.26.0", {"start": v(28.43, 29.04) * mm, "end": v(28.74, 28.74) * mm});
            skLineSegment(sketch, "E22.26.1", {"start": v(29.04, 28.43) * mm, "end": v(28.74, 28.74) * mm});
            skArc(sketch, "E22.26.2", {"start": v(29.17, 27.98) * mm, "mid": v(29.16, 28.22) * mm, "end": v(29.04, 28.43) * mm});
            skArc(sketch, "E22.26.3", {"start": v(28.43, 29.04) * mm, "mid": v(28.22, 29.16) * mm, "end": v(27.98, 29.17) * mm});
            skArc(sketch, "E22.26.4", {"start": v(25.8, 28.46) * mm, "mid": v(26.87, 28.88) * mm, "end": v(27.98, 29.17) * mm});
            skArc(sketch, "E22.26.5", {"start": v(28.46, 25.8) * mm, "mid": v(28.88, 26.87) * mm, "end": v(29.17, 27.98) * mm});
            skArc(sketch, "E22.26.6", {"start": v(28.08, 25.29) * mm, "mid": v(28.3, 25.52) * mm, "end": v(28.46, 25.8) * mm});
            skArc(sketch, "E22.26.7", {"start": v(25.8, 28.46) * mm, "mid": v(25.52, 28.3) * mm, "end": v(25.29, 28.08) * mm});
            skLineSegment(sketch, "E22.26.8", {"start": v(25.29, 28.08) * mm, "end": v(23.8, 26.43) * mm});
            skLineSegment(sketch, "E22.26.9", {"start": v(28.08, 25.29) * mm, "end": v(26.43, 23.8) * mm});
            skLineSegment(sketch, "E22.27.0", {"start": v(21.77, 34.32) * mm, "end": v(22.14, 34.09) * mm});
            skLineSegment(sketch, "E22.27.1", {"start": v(22.5, 33.85) * mm, "end": v(22.14, 34.09) * mm});
            skArc(sketch, "E22.27.2", {"start": v(22.72, 33.44) * mm, "mid": v(22.66, 33.67) * mm, "end": v(22.5, 33.85) * mm});
            skArc(sketch, "E22.27.3", {"start": v(21.77, 34.32) * mm, "mid": v(21.54, 34.4) * mm, "end": v(21.3, 34.35) * mm});
            skArc(sketch, "E22.27.4", {"start": v(19.32, 33.2) * mm, "mid": v(20.28, 33.84) * mm, "end": v(21.3, 34.35) * mm});
            skArc(sketch, "E22.27.5", {"start": v(22.48, 31.15) * mm, "mid": v(22.67, 32.29) * mm, "end": v(22.72, 33.44) * mm});
            skArc(sketch, "E22.27.6", {"start": v(22.21, 30.57) * mm, "mid": v(22.37, 30.85) * mm, "end": v(22.48, 31.15) * mm});
            skArc(sketch, "E22.27.7", {"start": v(19.32, 33.2) * mm, "mid": v(19.08, 32.99) * mm, "end": v(18.9, 32.73) * mm});
            skLineSegment(sketch, "E22.27.8", {"start": v(18.9, 32.73) * mm, "end": v(17.78, 30.8) * mm});
            skLineSegment(sketch, "E22.27.9", {"start": v(22.21, 30.57) * mm, "end": v(20.9, 28.77) * mm});
            skLineSegment(sketch, "E22.28.0", {"start": v(14.16, 38.1) * mm, "end": v(14.57, 37.95) * mm});
            skLineSegment(sketch, "E22.28.1", {"start": v(14.96, 37.79) * mm, "end": v(14.57, 37.95) * mm});
            skArc(sketch, "E22.28.2", {"start": v(15.27, 37.43) * mm, "mid": v(15.16, 37.64) * mm, "end": v(14.96, 37.79) * mm});
            skArc(sketch, "E22.28.3", {"start": v(14.16, 38.1) * mm, "mid": v(13.92, 38.12) * mm, "end": v(13.7, 38.03) * mm});
            skArc(sketch, "E22.28.4", {"start": v(12, 36.5) * mm, "mid": v(12.8, 37.32) * mm, "end": v(13.7, 38.03) * mm});
            skArc(sketch, "E22.28.5", {"start": v(15.5, 35.15) * mm, "mid": v(15.46, 36.3) * mm, "end": v(15.27, 37.43) * mm});
            skArc(sketch, "E22.28.6", {"start": v(15.37, 34.52) * mm, "mid": v(15.47, 34.83) * mm, "end": v(15.5, 35.15) * mm});
            skArc(sketch, "E22.28.7", {"start": v(12, 36.5) * mm, "mid": v(11.8, 36.23) * mm, "end": v(11.68, 35.94) * mm});
            skLineSegment(sketch, "E22.28.8", {"start": v(11.68, 35.94) * mm, "end": v(10.99, 33.82) * mm});
            skLineSegment(sketch, "E22.28.9", {"start": v(15.37, 34.52) * mm, "end": v(14.46, 32.49) * mm});
            skLineSegment(sketch, "E22.29.0", {"start": v(5.93, 40.2) * mm, "end": v(6.36, 40.15) * mm});
            skLineSegment(sketch, "E22.29.1", {"start": v(6.78, 40.07) * mm, "end": v(6.36, 40.15) * mm});
            skArc(sketch, "E22.29.2", {"start": v(7.15, 39.79) * mm, "mid": v(7, 39.97) * mm, "end": v(6.78, 40.07) * mm});
            skArc(sketch, "E22.29.3", {"start": v(5.93, 40.2) * mm, "mid": v(5.7, 40.18) * mm, "end": v(5.5, 40.05) * mm});
            skArc(sketch, "E22.29.4", {"start": v(4.14, 38.2) * mm, "mid": v(4.76, 39.16) * mm, "end": v(5.5, 40.05) * mm});
            skArc(sketch, "E22.29.5", {"start": v(7.86, 37.6) * mm, "mid": v(7.57, 38.72) * mm, "end": v(7.15, 39.79) * mm});
            skArc(sketch, "E22.29.6", {"start": v(7.86, 36.96) * mm, "mid": v(7.9, 37.28) * mm, "end": v(7.86, 37.6) * mm});
            skArc(sketch, "E22.29.7", {"start": v(4.14, 38.2) * mm, "mid": v(4.02, 37.9) * mm, "end": v(3.95, 37.58) * mm});
            skLineSegment(sketch, "E22.29.8", {"start": v(3.95, 37.58) * mm, "end": v(3.72, 35.37) * mm});
            skLineSegment(sketch, "E22.29.9", {"start": v(7.86, 36.96) * mm, "end": v(7.4, 34.78) * mm});
            skSolve(sketch);
        }
        {
            var Q0;
            Q0=makeQuery(id+"F0.imprint","IMPRINT",FACE,{"disambiguationData":[TD([[makeQuery(id+"F0.imprint","IMPRINT",EDGE,{"derivedFrom":sQuery(id+"F0.wireOp",EDGE,"E1.trimOffspring")}),1.0]])]});
            var Q1;
            Q1=makeQuery(id+"F2.imprint","IMPRINT",FACE,{"disambiguationData":[TD([[makeQuery(id+"F2.imprint","IMPRINT",EDGE,{"derivedFrom":sQuery(id+"F2.wireOp",EDGE,"E22.29.0")}),-1.0]])]});
            loft(context, id + "F3", {"sheetProfilesArray" : [{ "sheetProfileEntities" : qUnion([Q0]) }, { "sheetProfileEntities" : qUnion([Q1]) }]});
        }
        {
            var Q0;
            Q0=qCreatedBy(makeId("Front.planeOp"),FACE);
            var sketch = newSketch(context, id + "F4", { "sketchPlane" : qUnion([Q0])});
            skCircle(sketch, "E23", {"center": v(0, 0) * mm, "radius": 23.71 * mm});
            skSolve(sketch);
        }
        {
            var Q0;
            Q0=qCreatedBy(id+"F1.planeOp",FACE);
            var sketch = newSketch(context, id + "F5", { "sketchPlane" : qUnion([Q0])});
            skCircle(sketch, "E24", {"center": v(0, 0) * mm, "radius": 35.56 * mm});
            skSolve(sketch);
        }
        {
            var Q1;
            Q1=makeQuery(id+"F4.imprint","IMPRINT",FACE,{"disambiguationData":[TD([[makeQuery(id+"F4.imprint","IMPRINT",EDGE,{"derivedFrom":sQuery(id+"F4.wireOp",EDGE,"E23")}),1.0]])]});
            var Q2;
            Q2=makeQuery(id+"F5.imprint","IMPRINT",FACE,{"disambiguationData":[TD([[makeQuery(id+"F5.imprint","IMPRINT",EDGE,{"derivedFrom":sQuery(id+"F5.wireOp",EDGE,"E24")}),1.0]])]});
            loft(context, id + "F6", {"operationType" : NewBodyOperationType.ADD, "sheetProfilesArray" : [{ "sheetProfileEntities" : qUnion([Q1]) }, { "sheetProfileEntities" : qUnion([Q2]) }]});
        }
        {
            var Q0;
            Q0=makeQuery(id+"F3.opLoft","SWEPT_BODY",BODY,{"disambiguationData":[OSD([makeQuery(id+"F0.imprint","IMPRINT",FACE,{"disambiguationData":[TD([[makeQuery(id+"F0.imprint","IMPRINT",EDGE,{"derivedFrom":sQuery(id+"F0.wireOp",EDGE,"E1.trimOffspring")}),1.0]])]}),makeQuery(id+"F2.imprint","IMPRINT",FACE,{"disambiguationData":[TD([[makeQuery(id+"F2.imprint","IMPRINT",EDGE,{"derivedFrom":sQuery(id+"F2.wireOp",EDGE,"E22.29.0")}),-1.0]])]})])]});
            var Q1;
            Q1=makeQuery(id+"F6.opLoft","SWEPT_FACE",FACE,{"disambiguationData":[OSD([sQuery(id+"F4.wireOp",EDGE,"E23"),sQuery(id+"F5.wireOp",EDGE,"E24")])]});
            circularPattern(context, id + "F7", {"entities" : qUnion([Q0]), "axis" : qUnion([Q1]), "angle" : 360 * degree, "instanceCount" : 30, "equalSpace" : true});
        }
        {
            var Q0;
            Q0=makeQuery(id+"F3.opLoft","SWEPT_BODY",BODY,{"disambiguationData":[OSD([makeQuery(id+"F0.imprint","IMPRINT",FACE,{"disambiguationData":[TD([[makeQuery(id+"F0.imprint","IMPRINT",EDGE,{"derivedFrom":sQuery(id+"F0.wireOp",EDGE,"E1.trimOffspring")}),1.0]])]}),makeQuery(id+"F2.imprint","IMPRINT",FACE,{"disambiguationData":[TD([[makeQuery(id+"F2.imprint","IMPRINT",EDGE,{"derivedFrom":sQuery(id+"F2.wireOp",EDGE,"E22.29.0")}),-1.0]])]})])]});
            var Q1;
            Q1=makeQuery(id+"F7.opPattern","COPY",BODY,{"derivedFrom":makeQuery(id+"F3.opLoft","SWEPT_BODY",BODY,{"disambiguationData":[OSD([makeQuery(id+"F0.imprint","IMPRINT",FACE,{"disambiguationData":[TD([[makeQuery(id+"F0.imprint","IMPRINT",EDGE,{"derivedFrom":sQuery(id+"F0.wireOp",EDGE,"E1.trimOffspring")}),1.0]])]}),makeQuery(id+"F2.imprint","IMPRINT",FACE,{"disambiguationData":[TD([[makeQuery(id+"F2.imprint","IMPRINT",EDGE,{"derivedFrom":sQuery(id+"F2.wireOp",EDGE,"E22.29.0")}),-1.0]])]})])]}),"instanceName":"29"});
            var Q2;
            Q2=makeQuery(id+"F7.opPattern","COPY",BODY,{"derivedFrom":makeQuery(id+"F3.opLoft","SWEPT_BODY",BODY,{"disambiguationData":[OSD([makeQuery(id+"F0.imprint","IMPRINT",FACE,{"disambiguationData":[TD([[makeQuery(id+"F0.imprint","IMPRINT",EDGE,{"derivedFrom":sQuery(id+"F0.wireOp",EDGE,"E1.trimOffspring")}),1.0]])]}),makeQuery(id+"F2.imprint","IMPRINT",FACE,{"disambiguationData":[TD([[makeQuery(id+"F2.imprint","IMPRINT",EDGE,{"derivedFrom":sQuery(id+"F2.wireOp",EDGE,"E22.29.0")}),-1.0]])]})])]}),"instanceName":"28"});
            var Q3;
            Q3=makeQuery(id+"F7.opPattern","COPY",BODY,{"derivedFrom":makeQuery(id+"F3.opLoft","SWEPT_BODY",BODY,{"disambiguationData":[OSD([makeQuery(id+"F0.imprint","IMPRINT",FACE,{"disambiguationData":[TD([[makeQuery(id+"F0.imprint","IMPRINT",EDGE,{"derivedFrom":sQuery(id+"F0.wireOp",EDGE,"E1.trimOffspring")}),1.0]])]}),makeQuery(id+"F2.imprint","IMPRINT",FACE,{"disambiguationData":[TD([[makeQuery(id+"F2.imprint","IMPRINT",EDGE,{"derivedFrom":sQuery(id+"F2.wireOp",EDGE,"E22.29.0")}),-1.0]])]})])]}),"instanceName":"26"});
            var Q4;
            Q4=makeQuery(id+"F7.opPattern","COPY",BODY,{"derivedFrom":makeQuery(id+"F3.opLoft","SWEPT_BODY",BODY,{"disambiguationData":[OSD([makeQuery(id+"F0.imprint","IMPRINT",FACE,{"disambiguationData":[TD([[makeQuery(id+"F0.imprint","IMPRINT",EDGE,{"derivedFrom":sQuery(id+"F0.wireOp",EDGE,"E1.trimOffspring")}),1.0]])]}),makeQuery(id+"F2.imprint","IMPRINT",FACE,{"disambiguationData":[TD([[makeQuery(id+"F2.imprint","IMPRINT",EDGE,{"derivedFrom":sQuery(id+"F2.wireOp",EDGE,"E22.29.0")}),-1.0]])]})])]}),"instanceName":"25"});
            var Q5;
            Q5=makeQuery(id+"F7.opPattern","COPY",BODY,{"derivedFrom":makeQuery(id+"F3.opLoft","SWEPT_BODY",BODY,{"disambiguationData":[OSD([makeQuery(id+"F0.imprint","IMPRINT",FACE,{"disambiguationData":[TD([[makeQuery(id+"F0.imprint","IMPRINT",EDGE,{"derivedFrom":sQuery(id+"F0.wireOp",EDGE,"E1.trimOffspring")}),1.0]])]}),makeQuery(id+"F2.imprint","IMPRINT",FACE,{"disambiguationData":[TD([[makeQuery(id+"F2.imprint","IMPRINT",EDGE,{"derivedFrom":sQuery(id+"F2.wireOp",EDGE,"E22.29.0")}),-1.0]])]})])]}),"instanceName":"24"});
            var Q6;
            Q6=makeQuery(id+"F7.opPattern","COPY",BODY,{"derivedFrom":makeQuery(id+"F3.opLoft","SWEPT_BODY",BODY,{"disambiguationData":[OSD([makeQuery(id+"F0.imprint","IMPRINT",FACE,{"disambiguationData":[TD([[makeQuery(id+"F0.imprint","IMPRINT",EDGE,{"derivedFrom":sQuery(id+"F0.wireOp",EDGE,"E1.trimOffspring")}),1.0]])]}),makeQuery(id+"F2.imprint","IMPRINT",FACE,{"disambiguationData":[TD([[makeQuery(id+"F2.imprint","IMPRINT",EDGE,{"derivedFrom":sQuery(id+"F2.wireOp",EDGE,"E22.29.0")}),-1.0]])]})])]}),"instanceName":"23"});
            var Q7;
            Q7=makeQuery(id+"F7.opPattern","COPY",BODY,{"derivedFrom":makeQuery(id+"F3.opLoft","SWEPT_BODY",BODY,{"disambiguationData":[OSD([makeQuery(id+"F0.imprint","IMPRINT",FACE,{"disambiguationData":[TD([[makeQuery(id+"F0.imprint","IMPRINT",EDGE,{"derivedFrom":sQuery(id+"F0.wireOp",EDGE,"E1.trimOffspring")}),1.0]])]}),makeQuery(id+"F2.imprint","IMPRINT",FACE,{"disambiguationData":[TD([[makeQuery(id+"F2.imprint","IMPRINT",EDGE,{"derivedFrom":sQuery(id+"F2.wireOp",EDGE,"E22.29.0")}),-1.0]])]})])]}),"instanceName":"22"});
            var Q8;
            Q8=makeQuery(id+"F7.opPattern","COPY",BODY,{"derivedFrom":makeQuery(id+"F3.opLoft","SWEPT_BODY",BODY,{"disambiguationData":[OSD([makeQuery(id+"F0.imprint","IMPRINT",FACE,{"disambiguationData":[TD([[makeQuery(id+"F0.imprint","IMPRINT",EDGE,{"derivedFrom":sQuery(id+"F0.wireOp",EDGE,"E1.trimOffspring")}),1.0]])]}),makeQuery(id+"F2.imprint","IMPRINT",FACE,{"disambiguationData":[TD([[makeQuery(id+"F2.imprint","IMPRINT",EDGE,{"derivedFrom":sQuery(id+"F2.wireOp",EDGE,"E22.29.0")}),-1.0]])]})])]}),"instanceName":"21"});
            var Q9;
            Q9=makeQuery(id+"F7.opPattern","COPY",BODY,{"derivedFrom":makeQuery(id+"F3.opLoft","SWEPT_BODY",BODY,{"disambiguationData":[OSD([makeQuery(id+"F0.imprint","IMPRINT",FACE,{"disambiguationData":[TD([[makeQuery(id+"F0.imprint","IMPRINT",EDGE,{"derivedFrom":sQuery(id+"F0.wireOp",EDGE,"E1.trimOffspring")}),1.0]])]}),makeQuery(id+"F2.imprint","IMPRINT",FACE,{"disambiguationData":[TD([[makeQuery(id+"F2.imprint","IMPRINT",EDGE,{"derivedFrom":sQuery(id+"F2.wireOp",EDGE,"E22.29.0")}),-1.0]])]})])]}),"instanceName":"20"});
            var Q10;
            Q10=makeQuery(id+"F7.opPattern","COPY",BODY,{"derivedFrom":makeQuery(id+"F3.opLoft","SWEPT_BODY",BODY,{"disambiguationData":[OSD([makeQuery(id+"F0.imprint","IMPRINT",FACE,{"disambiguationData":[TD([[makeQuery(id+"F0.imprint","IMPRINT",EDGE,{"derivedFrom":sQuery(id+"F0.wireOp",EDGE,"E1.trimOffspring")}),1.0]])]}),makeQuery(id+"F2.imprint","IMPRINT",FACE,{"disambiguationData":[TD([[makeQuery(id+"F2.imprint","IMPRINT",EDGE,{"derivedFrom":sQuery(id+"F2.wireOp",EDGE,"E22.29.0")}),-1.0]])]})])]}),"instanceName":"19"});
            var Q11;
            Q11=makeQuery(id+"F7.opPattern","COPY",BODY,{"derivedFrom":makeQuery(id+"F3.opLoft","SWEPT_BODY",BODY,{"disambiguationData":[OSD([makeQuery(id+"F0.imprint","IMPRINT",FACE,{"disambiguationData":[TD([[makeQuery(id+"F0.imprint","IMPRINT",EDGE,{"derivedFrom":sQuery(id+"F0.wireOp",EDGE,"E1.trimOffspring")}),1.0]])]}),makeQuery(id+"F2.imprint","IMPRINT",FACE,{"disambiguationData":[TD([[makeQuery(id+"F2.imprint","IMPRINT",EDGE,{"derivedFrom":sQuery(id+"F2.wireOp",EDGE,"E22.29.0")}),-1.0]])]})])]}),"instanceName":"18"});
            var Q12;
            Q12=makeQuery(id+"F7.opPattern","COPY",BODY,{"derivedFrom":makeQuery(id+"F3.opLoft","SWEPT_BODY",BODY,{"disambiguationData":[OSD([makeQuery(id+"F0.imprint","IMPRINT",FACE,{"disambiguationData":[TD([[makeQuery(id+"F0.imprint","IMPRINT",EDGE,{"derivedFrom":sQuery(id+"F0.wireOp",EDGE,"E1.trimOffspring")}),1.0]])]}),makeQuery(id+"F2.imprint","IMPRINT",FACE,{"disambiguationData":[TD([[makeQuery(id+"F2.imprint","IMPRINT",EDGE,{"derivedFrom":sQuery(id+"F2.wireOp",EDGE,"E22.29.0")}),-1.0]])]})])]}),"instanceName":"17"});
            var Q13;
            Q13=makeQuery(id+"F7.opPattern","COPY",BODY,{"derivedFrom":makeQuery(id+"F3.opLoft","SWEPT_BODY",BODY,{"disambiguationData":[OSD([makeQuery(id+"F0.imprint","IMPRINT",FACE,{"disambiguationData":[TD([[makeQuery(id+"F0.imprint","IMPRINT",EDGE,{"derivedFrom":sQuery(id+"F0.wireOp",EDGE,"E1.trimOffspring")}),1.0]])]}),makeQuery(id+"F2.imprint","IMPRINT",FACE,{"disambiguationData":[TD([[makeQuery(id+"F2.imprint","IMPRINT",EDGE,{"derivedFrom":sQuery(id+"F2.wireOp",EDGE,"E22.29.0")}),-1.0]])]})])]}),"instanceName":"16"});
            var Q14;
            Q14=makeQuery(id+"F7.opPattern","COPY",BODY,{"derivedFrom":makeQuery(id+"F3.opLoft","SWEPT_BODY",BODY,{"disambiguationData":[OSD([makeQuery(id+"F0.imprint","IMPRINT",FACE,{"disambiguationData":[TD([[makeQuery(id+"F0.imprint","IMPRINT",EDGE,{"derivedFrom":sQuery(id+"F0.wireOp",EDGE,"E1.trimOffspring")}),1.0]])]}),makeQuery(id+"F2.imprint","IMPRINT",FACE,{"disambiguationData":[TD([[makeQuery(id+"F2.imprint","IMPRINT",EDGE,{"derivedFrom":sQuery(id+"F2.wireOp",EDGE,"E22.29.0")}),-1.0]])]})])]}),"instanceName":"15"});
            var Q15;
            Q15=makeQuery(id+"F7.opPattern","COPY",BODY,{"derivedFrom":makeQuery(id+"F3.opLoft","SWEPT_BODY",BODY,{"disambiguationData":[OSD([makeQuery(id+"F0.imprint","IMPRINT",FACE,{"disambiguationData":[TD([[makeQuery(id+"F0.imprint","IMPRINT",EDGE,{"derivedFrom":sQuery(id+"F0.wireOp",EDGE,"E1.trimOffspring")}),1.0]])]}),makeQuery(id+"F2.imprint","IMPRINT",FACE,{"disambiguationData":[TD([[makeQuery(id+"F2.imprint","IMPRINT",EDGE,{"derivedFrom":sQuery(id+"F2.wireOp",EDGE,"E22.29.0")}),-1.0]])]})])]}),"instanceName":"14"});
            var Q16;
            Q16=makeQuery(id+"F7.opPattern","COPY",BODY,{"derivedFrom":makeQuery(id+"F3.opLoft","SWEPT_BODY",BODY,{"disambiguationData":[OSD([makeQuery(id+"F0.imprint","IMPRINT",FACE,{"disambiguationData":[TD([[makeQuery(id+"F0.imprint","IMPRINT",EDGE,{"derivedFrom":sQuery(id+"F0.wireOp",EDGE,"E1.trimOffspring")}),1.0]])]}),makeQuery(id+"F2.imprint","IMPRINT",FACE,{"disambiguationData":[TD([[makeQuery(id+"F2.imprint","IMPRINT",EDGE,{"derivedFrom":sQuery(id+"F2.wireOp",EDGE,"E22.29.0")}),-1.0]])]})])]}),"instanceName":"13"});
            var Q17;
            Q17=makeQuery(id+"F7.opPattern","COPY",BODY,{"derivedFrom":makeQuery(id+"F3.opLoft","SWEPT_BODY",BODY,{"disambiguationData":[OSD([makeQuery(id+"F0.imprint","IMPRINT",FACE,{"disambiguationData":[TD([[makeQuery(id+"F0.imprint","IMPRINT",EDGE,{"derivedFrom":sQuery(id+"F0.wireOp",EDGE,"E1.trimOffspring")}),1.0]])]}),makeQuery(id+"F2.imprint","IMPRINT",FACE,{"disambiguationData":[TD([[makeQuery(id+"F2.imprint","IMPRINT",EDGE,{"derivedFrom":sQuery(id+"F2.wireOp",EDGE,"E22.29.0")}),-1.0]])]})])]}),"instanceName":"12"});
            var Q18;
            Q18=makeQuery(id+"F7.opPattern","COPY",BODY,{"derivedFrom":makeQuery(id+"F3.opLoft","SWEPT_BODY",BODY,{"disambiguationData":[OSD([makeQuery(id+"F0.imprint","IMPRINT",FACE,{"disambiguationData":[TD([[makeQuery(id+"F0.imprint","IMPRINT",EDGE,{"derivedFrom":sQuery(id+"F0.wireOp",EDGE,"E1.trimOffspring")}),1.0]])]}),makeQuery(id+"F2.imprint","IMPRINT",FACE,{"disambiguationData":[TD([[makeQuery(id+"F2.imprint","IMPRINT",EDGE,{"derivedFrom":sQuery(id+"F2.wireOp",EDGE,"E22.29.0")}),-1.0]])]})])]}),"instanceName":"11"});
            var Q19;
            Q19=makeQuery(id+"F7.opPattern","COPY",BODY,{"derivedFrom":makeQuery(id+"F3.opLoft","SWEPT_BODY",BODY,{"disambiguationData":[OSD([makeQuery(id+"F0.imprint","IMPRINT",FACE,{"disambiguationData":[TD([[makeQuery(id+"F0.imprint","IMPRINT",EDGE,{"derivedFrom":sQuery(id+"F0.wireOp",EDGE,"E1.trimOffspring")}),1.0]])]}),makeQuery(id+"F2.imprint","IMPRINT",FACE,{"disambiguationData":[TD([[makeQuery(id+"F2.imprint","IMPRINT",EDGE,{"derivedFrom":sQuery(id+"F2.wireOp",EDGE,"E22.29.0")}),-1.0]])]})])]}),"instanceName":"10"});
            var Q20;
            Q20=makeQuery(id+"F7.opPattern","COPY",BODY,{"derivedFrom":makeQuery(id+"F3.opLoft","SWEPT_BODY",BODY,{"disambiguationData":[OSD([makeQuery(id+"F0.imprint","IMPRINT",FACE,{"disambiguationData":[TD([[makeQuery(id+"F0.imprint","IMPRINT",EDGE,{"derivedFrom":sQuery(id+"F0.wireOp",EDGE,"E1.trimOffspring")}),1.0]])]}),makeQuery(id+"F2.imprint","IMPRINT",FACE,{"disambiguationData":[TD([[makeQuery(id+"F2.imprint","IMPRINT",EDGE,{"derivedFrom":sQuery(id+"F2.wireOp",EDGE,"E22.29.0")}),-1.0]])]})])]}),"instanceName":"27"});
            var Q21;
            Q21=makeQuery(id+"F7.opPattern","COPY",BODY,{"derivedFrom":makeQuery(id+"F3.opLoft","SWEPT_BODY",BODY,{"disambiguationData":[OSD([makeQuery(id+"F0.imprint","IMPRINT",FACE,{"disambiguationData":[TD([[makeQuery(id+"F0.imprint","IMPRINT",EDGE,{"derivedFrom":sQuery(id+"F0.wireOp",EDGE,"E1.trimOffspring")}),1.0]])]}),makeQuery(id+"F2.imprint","IMPRINT",FACE,{"disambiguationData":[TD([[makeQuery(id+"F2.imprint","IMPRINT",EDGE,{"derivedFrom":sQuery(id+"F2.wireOp",EDGE,"E22.29.0")}),-1.0]])]})])]}),"instanceName":"8"});
            var Q22;
            Q22=makeQuery(id+"F7.opPattern","COPY",BODY,{"derivedFrom":makeQuery(id+"F3.opLoft","SWEPT_BODY",BODY,{"disambiguationData":[OSD([makeQuery(id+"F0.imprint","IMPRINT",FACE,{"disambiguationData":[TD([[makeQuery(id+"F0.imprint","IMPRINT",EDGE,{"derivedFrom":sQuery(id+"F0.wireOp",EDGE,"E1.trimOffspring")}),1.0]])]}),makeQuery(id+"F2.imprint","IMPRINT",FACE,{"disambiguationData":[TD([[makeQuery(id+"F2.imprint","IMPRINT",EDGE,{"derivedFrom":sQuery(id+"F2.wireOp",EDGE,"E22.29.0")}),-1.0]])]})])]}),"instanceName":"9"});
            var Q23;
            Q23=makeQuery(id+"F7.opPattern","COPY",BODY,{"derivedFrom":makeQuery(id+"F3.opLoft","SWEPT_BODY",BODY,{"disambiguationData":[OSD([makeQuery(id+"F0.imprint","IMPRINT",FACE,{"disambiguationData":[TD([[makeQuery(id+"F0.imprint","IMPRINT",EDGE,{"derivedFrom":sQuery(id+"F0.wireOp",EDGE,"E1.trimOffspring")}),1.0]])]}),makeQuery(id+"F2.imprint","IMPRINT",FACE,{"disambiguationData":[TD([[makeQuery(id+"F2.imprint","IMPRINT",EDGE,{"derivedFrom":sQuery(id+"F2.wireOp",EDGE,"E22.29.0")}),-1.0]])]})])]}),"instanceName":"7"});
            var Q24;
            Q24=makeQuery(id+"F7.opPattern","COPY",BODY,{"derivedFrom":makeQuery(id+"F3.opLoft","SWEPT_BODY",BODY,{"disambiguationData":[OSD([makeQuery(id+"F0.imprint","IMPRINT",FACE,{"disambiguationData":[TD([[makeQuery(id+"F0.imprint","IMPRINT",EDGE,{"derivedFrom":sQuery(id+"F0.wireOp",EDGE,"E1.trimOffspring")}),1.0]])]}),makeQuery(id+"F2.imprint","IMPRINT",FACE,{"disambiguationData":[TD([[makeQuery(id+"F2.imprint","IMPRINT",EDGE,{"derivedFrom":sQuery(id+"F2.wireOp",EDGE,"E22.29.0")}),-1.0]])]})])]}),"instanceName":"6"});
            var Q25;
            Q25=makeQuery(id+"F7.opPattern","COPY",BODY,{"derivedFrom":makeQuery(id+"F3.opLoft","SWEPT_BODY",BODY,{"disambiguationData":[OSD([makeQuery(id+"F0.imprint","IMPRINT",FACE,{"disambiguationData":[TD([[makeQuery(id+"F0.imprint","IMPRINT",EDGE,{"derivedFrom":sQuery(id+"F0.wireOp",EDGE,"E1.trimOffspring")}),1.0]])]}),makeQuery(id+"F2.imprint","IMPRINT",FACE,{"disambiguationData":[TD([[makeQuery(id+"F2.imprint","IMPRINT",EDGE,{"derivedFrom":sQuery(id+"F2.wireOp",EDGE,"E22.29.0")}),-1.0]])]})])]}),"instanceName":"5"});
            var Q26;
            Q26=makeQuery(id+"F7.opPattern","COPY",BODY,{"derivedFrom":makeQuery(id+"F3.opLoft","SWEPT_BODY",BODY,{"disambiguationData":[OSD([makeQuery(id+"F0.imprint","IMPRINT",FACE,{"disambiguationData":[TD([[makeQuery(id+"F0.imprint","IMPRINT",EDGE,{"derivedFrom":sQuery(id+"F0.wireOp",EDGE,"E1.trimOffspring")}),1.0]])]}),makeQuery(id+"F2.imprint","IMPRINT",FACE,{"disambiguationData":[TD([[makeQuery(id+"F2.imprint","IMPRINT",EDGE,{"derivedFrom":sQuery(id+"F2.wireOp",EDGE,"E22.29.0")}),-1.0]])]})])]}),"instanceName":"4"});
            var Q27;
            Q27=makeQuery(id+"F7.opPattern","COPY",BODY,{"derivedFrom":makeQuery(id+"F3.opLoft","SWEPT_BODY",BODY,{"disambiguationData":[OSD([makeQuery(id+"F0.imprint","IMPRINT",FACE,{"disambiguationData":[TD([[makeQuery(id+"F0.imprint","IMPRINT",EDGE,{"derivedFrom":sQuery(id+"F0.wireOp",EDGE,"E1.trimOffspring")}),1.0]])]}),makeQuery(id+"F2.imprint","IMPRINT",FACE,{"disambiguationData":[TD([[makeQuery(id+"F2.imprint","IMPRINT",EDGE,{"derivedFrom":sQuery(id+"F2.wireOp",EDGE,"E22.29.0")}),-1.0]])]})])]}),"instanceName":"3"});
            var Q28;
            Q28=makeQuery(id+"F7.opPattern","COPY",BODY,{"derivedFrom":makeQuery(id+"F3.opLoft","SWEPT_BODY",BODY,{"disambiguationData":[OSD([makeQuery(id+"F0.imprint","IMPRINT",FACE,{"disambiguationData":[TD([[makeQuery(id+"F0.imprint","IMPRINT",EDGE,{"derivedFrom":sQuery(id+"F0.wireOp",EDGE,"E1.trimOffspring")}),1.0]])]}),makeQuery(id+"F2.imprint","IMPRINT",FACE,{"disambiguationData":[TD([[makeQuery(id+"F2.imprint","IMPRINT",EDGE,{"derivedFrom":sQuery(id+"F2.wireOp",EDGE,"E22.29.0")}),-1.0]])]})])]}),"instanceName":"2"});
            var Q29;
            Q29=makeQuery(id+"F7.opPattern","COPY",BODY,{"derivedFrom":makeQuery(id+"F3.opLoft","SWEPT_BODY",BODY,{"disambiguationData":[OSD([makeQuery(id+"F0.imprint","IMPRINT",FACE,{"disambiguationData":[TD([[makeQuery(id+"F0.imprint","IMPRINT",EDGE,{"derivedFrom":sQuery(id+"F0.wireOp",EDGE,"E1.trimOffspring")}),1.0]])]}),makeQuery(id+"F2.imprint","IMPRINT",FACE,{"disambiguationData":[TD([[makeQuery(id+"F2.imprint","IMPRINT",EDGE,{"derivedFrom":sQuery(id+"F2.wireOp",EDGE,"E22.29.0")}),-1.0]])]})])]}),"instanceName":"1"});
            booleanBodies(context, id + "F8", {"operationType" : BooleanOperationType.UNION, "tools" : qUnion([Q0, Q1, Q2, Q3, Q4, Q5, Q6, Q7, Q8, Q9, Q10, Q11, Q12, Q13, Q14, Q15, Q16, Q17, Q18, Q19, Q20, Q21, Q22, Q23, Q24, Q25, Q26, Q27, Q28, Q29])});
        }
        {
            var Q0;
            {var subQ3=makeQuery(id+"F6.boolean.opBoolean","MERGE",FACE,{"derivedFrom":[makeQuery(id+"F3.opLoft","CAP_FACE",FACE,{"disambiguationData":[OSD([makeQuery(id+"F2.imprint","IMPRINT",FACE,{"disambiguationData":[TD([[makeQuery(id+"F2.imprint","IMPRINT",EDGE,{"derivedFrom":sQuery(id+"F2.wireOp",EDGE,"E22.29.0")}),-1.0]])]})])],"isStart":true}),makeQuery(id+"F6.opLoft","CAP_FACE",FACE,{"disambiguationData":[OSD([makeQuery(id+"F5.imprint","IMPRINT",FACE,{"disambiguationData":[TD([[makeQuery(id+"F5.imprint","IMPRINT",EDGE,{"derivedFrom":sQuery(id+"F5.wireOp",EDGE,"E24")}),1.0]])]})])],"isStart":true})]});Q0=makeQuery(id+"F8.opBoolean","MERGE",FACE,{"derivedFrom":[subQ3,makeQuery(id+"F7.opPattern","COPY",FACE,{"derivedFrom":subQ3,"instanceName":"1"}),makeQuery(id+"F7.opPattern","COPY",FACE,{"derivedFrom":subQ3,"instanceName":"2"}),makeQuery(id+"F7.opPattern","COPY",FACE,{"derivedFrom":subQ3,"instanceName":"3"}),makeQuery(id+"F7.opPattern","COPY",FACE,{"derivedFrom":subQ3,"instanceName":"4"}),makeQuery(id+"F7.opPattern","COPY",FACE,{"derivedFrom":subQ3,"instanceName":"5"}),makeQuery(id+"F7.opPattern","COPY",FACE,{"derivedFrom":subQ3,"instanceName":"6"}),makeQuery(id+"F7.opPattern","COPY",FACE,{"derivedFrom":subQ3,"instanceName":"7"}),makeQuery(id+"F7.opPattern","COPY",FACE,{"derivedFrom":subQ3,"instanceName":"8"}),makeQuery(id+"F7.opPattern","COPY",FACE,{"derivedFrom":subQ3,"instanceName":"9"}),makeQuery(id+"F7.opPattern","COPY",FACE,{"derivedFrom":subQ3,"instanceName":"10"}),makeQuery(id+"F7.opPattern","COPY",FACE,{"derivedFrom":subQ3,"instanceName":"11"}),makeQuery(id+"F7.opPattern","COPY",FACE,{"derivedFrom":subQ3,"instanceName":"12"}),makeQuery(id+"F7.opPattern","COPY",FACE,{"derivedFrom":subQ3,"instanceName":"13"}),makeQuery(id+"F7.opPattern","COPY",FACE,{"derivedFrom":subQ3,"instanceName":"14"}),makeQuery(id+"F7.opPattern","COPY",FACE,{"derivedFrom":subQ3,"instanceName":"15"}),makeQuery(id+"F7.opPattern","COPY",FACE,{"derivedFrom":subQ3,"instanceName":"16"}),makeQuery(id+"F7.opPattern","COPY",FACE,{"derivedFrom":subQ3,"instanceName":"17"}),makeQuery(id+"F7.opPattern","COPY",FACE,{"derivedFrom":subQ3,"instanceName":"18"}),makeQuery(id+"F7.opPattern","COPY",FACE,{"derivedFrom":subQ3,"instanceName":"19"}),makeQuery(id+"F7.opPattern","COPY",FACE,{"derivedFrom":subQ3,"instanceName":"20"}),makeQuery(id+"F7.opPattern","COPY",FACE,{"derivedFrom":subQ3,"instanceName":"21"}),makeQuery(id+"F7.opPattern","COPY",FACE,{"derivedFrom":subQ3,"instanceName":"22"}),makeQuery(id+"F7.opPattern","COPY",FACE,{"derivedFrom":subQ3,"instanceName":"23"}),makeQuery(id+"F7.opPattern","COPY",FACE,{"derivedFrom":subQ3,"instanceName":"24"}),makeQuery(id+"F7.opPattern","COPY",FACE,{"derivedFrom":subQ3,"instanceName":"25"}),makeQuery(id+"F7.opPattern","COPY",FACE,{"derivedFrom":subQ3,"instanceName":"26"}),makeQuery(id+"F7.opPattern","COPY",FACE,{"derivedFrom":subQ3,"instanceName":"27"}),makeQuery(id+"F7.opPattern","COPY",FACE,{"derivedFrom":subQ3,"instanceName":"28"}),makeQuery(id+"F7.opPattern","COPY",FACE,{"derivedFrom":subQ3,"instanceName":"29"})]});}
            var sketch = newSketch(context, id + "F9", { "sketchPlane" : qUnion([Q0])});
            skCircle(sketch, "E25", {"center": v(0, 0) * mm, "radius": 6.35 * mm});
            skSolve(sketch);
        }
        {
            var Q0;
            Q0 = qSketchRegion(id + "F9", true);
            extrude(context, id + "F10", {"entities" : qUnion([Q0]), "operationType" : NewBodyOperationType.REMOVE, "endBound" : BoundingType.THROUGH_ALL, "oppositeDirection" : true, "depth" : 25.4 * mm});
        }
    });
